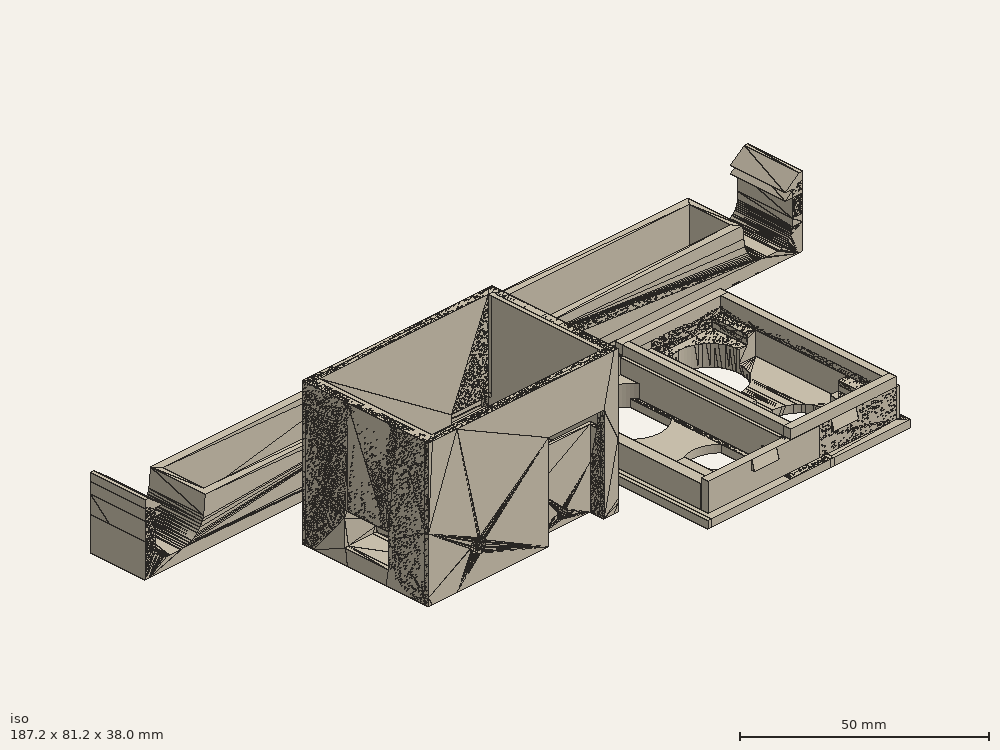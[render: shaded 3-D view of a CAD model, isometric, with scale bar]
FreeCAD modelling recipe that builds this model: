
FCSTD DOCUMENT  (FreeCAD 0.18.4R)
Label: station.sensor
License: All rights reserved
LicenseURL: http://en.wikipedia.org/wiki/All_rights_reserved
objects: Part::Extrusion×50, Part::Feature×48, Part::MultiFuse×25, Part::Cut×23, Part::Part2DObjectPython×19, Part::FeaturePython×15, App::DocumentObjectGroup×5
note: 180 computed .brp shape members not serialized (recipe doc carries the construction recipe); baked Part::Feature solids carry a one-line shape summary decoded from their .brp

FEATURE [Part::Feature] Cut004008021006004001003001  label="Cut004008021006004001004"
  shape: bbox 187.2 x 15.6 x 18.67 mm, 52 faces, 2 solids (baked)
FEATURE [Part::Feature] Fusion005002002014004003003002009002010004002003006003008008004007002004008002005003003004013003004015001  label="Fusion005002002014004003003002009002010004002003006003008008004007002004008002005003003004013003004019"
  shape: bbox 54 x 34.03 x 38 mm, 82 faces (baked)
FEATURE [Part::Feature] Cut004008021006004001001  label="Cut004008021006006"
  shape: bbox 34.03 x 54 x 8 mm, 44 faces (baked)
FEATURE [Part::Part2DObjectPython] Wire  # Draft 2D object (typed FeaturePython)
  ChamferSize = 0
  Closed = true
  End = (195.757,-75.1327,-187.001)
  FilletRadius = 0
  Length = 25.2
  MakeFace = true
  Placement = pos=(193.657,-71.4954,-187.001) rot=(0,0,1;0rad)
  Points = (6) [(0,0,0),(2.1,3.63731,0),(6.3,3.63731,0),(8.4,0,0),(6.3,-3.63731,0),(2.1,-3.63731,2.84217e-14)]
  Start = (193.657,-71.4954,-187.001)
  Subdivisions = 0
FEATURE [Part::Feature] Face
  shape: bbox 10 x 11.6 x 0.0004728 mm, 1 faces, 0 solids (baked)
FEATURE [Part::Extrusion] Extrusion
  Base = -> Face
  Dir = (3e-15,1.7e-14,1)
  DirMode = 0
  FaceMakerClass = Part::FaceMakerBullseye
  LengthFwd = 0
  LengthRev = 0
  Solid = true
  Symmetric = false
FEATURE [Part::Cut] Cut
  Base = -> Cut004008021006004001003001
  Tool = -> Extrusion
FEATURE [Part::Feature] Face001
  Placement = pos=(3e-15,1.7e-14,1) rot=(0,0,1;0rad)
  shape: bbox 10 x 11.6 x 0.0004728 mm, 1 faces, 0 solids (baked)
FEATURE [Part::Extrusion] Extrusion001
  Base = -> Face001
  Dir = (-1.05e-14,-5.95e-14,-3.5)
  DirMode = 0
  FaceMakerClass = Part::FaceMakerBullseye
  LengthFwd = 0
  LengthRev = 0
  Solid = true
  Symmetric = false
FEATURE [Part::Extrusion] Extrusion002
  Base = -> Wire
  Dir = (3.9e-15,8.4e-15,3.5)
  DirMode = 0
  FaceMakerClass = Part::FaceMakerBullseye
  LengthFwd = 0
  LengthRev = 0
  Solid = true
  Symmetric = false
FEATURE [Part::Cut] Cut004008021006004001003002
  Base = -> Extrusion001
  Tool = -> Extrusion002
FEATURE [Part::MultiFuse] Fusion
  Shapes = -> [Cut004008021006004001003002,Cut]
FEATURE [Part::Part2DObjectPython] Rectangle  # Draft 2D object (typed FeaturePython)
  ChamferSize = 0
  Columns = 1
  FilletRadius = 0
  Height = 2.16
  Length = 2.16
  MakeFace = true
  Placement = pos=(202.857,-77.2954,-189.161) rot=(0.57735,0.57735,0.57735;2.0944rad)
  Rows = 1
  Support = -> [Fusion]
FEATURE [Part::Extrusion] Extrusion003
  Base = -> Rectangle
  Dir = (-10,0,0)
  DirMode = 0
  FaceMakerClass = Part::FaceMakerBullseye
  LengthFwd = 0
  LengthRev = 0
  Placement = pos=(0,9.44,-1.99e-13) rot=(0,0,1;0rad)
  Solid = true
  Symmetric = false
FEATURE [Part::Extrusion] Extrusion004
  Base = -> Rectangle
  Dir = (-10,0,0)
  DirMode = 0
  FaceMakerClass = Part::FaceMakerBullseye
  LengthFwd = 0
  LengthRev = 0
  Solid = true
  Symmetric = false
FEATURE [Part::Part2DObjectPython] Circle  # Draft 2D object (typed FeaturePython)
  FirstAngle = 0
  LastAngle = 0
  MakeFace = true
  Placement = pos=(202.857,-67.8554,-189.161) rot=(0.57735,0.57735,0.57735;2.0944rad)
  Radius = 2.16
  Support = -> [Extrusion003]
FEATURE [Part::Extrusion] Extrusion005
  Base = -> Circle
  Dir = (-10,0,0)
  DirMode = 0
  FaceMakerClass = Part::FaceMakerBullseye
  LengthFwd = 0
  LengthRev = 0
  Solid = true
  Symmetric = false
FEATURE [Part::Extrusion] Extrusion006
  Base = -> Circle
  Dir = (-10,0,0)
  DirMode = 0
  FaceMakerClass = Part::FaceMakerBullseye
  LengthFwd = 0
  LengthRev = 0
  Placement = pos=(0,-7.28,1.99e-13) rot=(0,0,1;0rad)
  Solid = true
  Symmetric = false
FEATURE [Part::Cut] Cut004008021006004001003003
  Base = -> Extrusion003
  Tool = -> Extrusion005
FEATURE [Part::Cut] Cut004008021006004001003004
  Base = -> Extrusion004
  Tool = -> Extrusion006
FEATURE [Part::MultiFuse] Fusion005002002014004003003002009002010004002003006003008008004007002004008002005003003004013003004015002
  Placement = pos=(-5.94964,-41.2662,-1.6816e-09) rot=(0,0,1;0rad)
  Shapes = -> [Cut004008021006004001003003,Cut004008021006004001003004,Fusion]
FEATURE [Part::Part2DObjectPython] Rectangle001  # Draft 2D object (typed FeaturePython)
  ChamferSize = 0
  Columns = 1
  FilletRadius = 0
  Height = 2
  Length = 21
  MakeFace = true
  Placement = pos=(223.104,-136.121,-186.001) rot=(0,0,1;0rad)
  Rows = 1
FEATURE [Part::Extrusion] Extrusion007
  Base = -> Rectangle001
  Dir = (3e-16,0,-3.5)
  DirMode = 0
  FaceMakerClass = Part::FaceMakerBullseye
  LengthFwd = 0
  LengthRev = 0
  Solid = true
  Symmetric = false
FEATURE [Part::Feature] Face002
  Placement = pos=(223.104,-136.121,-186.001) rot=(0,0,1;0rad)
  shape: bbox 21 x 2 x 2e-07 mm, 1 faces, 0 solids (baked)
FEATURE [Part::Extrusion] Extrusion008
  Base = -> Face002
  Dir = (-2e-16,0,2.5)
  DirMode = 0
  FaceMakerClass = Part::FaceMakerBullseye
  LengthFwd = 0
  LengthRev = 0
  Solid = true
  Symmetric = false
FEATURE [Part::MultiFuse] Fusion005002002014004003003002009002010004002003006003008008004007002004008002005003003004013003004015003
  Shapes = -> [Extrusion008,Extrusion007]
FEATURE [Part::Feature] Fusion005002002014004003003002009002010004002003006003008008004007002004008002005003003004013003004015003001  label="Fusion005002002014004003003002009002010004002003006003008008004007002004008002005003003004013003004015004"
  shape: bbox 21 x 2 x 6 mm, 6 faces (baked)
FEATURE [Part::Feature] Face003
  shape: bbox 2e-07 x 2 x 6 mm, 1 faces, 0 solids (baked)
FEATURE [Part::Extrusion] Extrusion009
  Base = -> Face003
  Dir = (4.51897,0,0)
  DirMode = 0
  FaceMakerClass = Part::FaceMakerBullseye
  LengthFwd = 0
  LengthRev = 0
  Solid = true
  Symmetric = false
FEATURE [Part::Feature] Face004
  shape: bbox 2e-07 x 2 x 6 mm, 1 faces, 0 solids (baked)
FEATURE [Part::Extrusion] Extrusion010
  Base = -> Face004
  Dir = (-4.50603,0,0)
  DirMode = 0
  FaceMakerClass = Part::FaceMakerBullseye
  LengthFwd = 0
  LengthRev = 0
  Solid = true
  Symmetric = false
FEATURE [Part::MultiFuse] Fusion005002002014004003003002009002010004002003006003008008004007002004008002005003003004013003004015003002
  Shapes = -> [Fusion005002002014004003003002009002010004002003006003008008004007002004008002005003003004013003004015003001,Extrusion010,Extrusion009]
FEATURE [Part::Feature] Fusion005002002014004003003002009002010004002003006003008008004007002004008002005003003004013003004015003002001  label="Fusion005002002014004003003002009002010004002003006003008008004007002004008002005003003004013003004015003003"
  Placement = pos=(0,-48,0) rot=(0,0,1;0rad)
  shape: bbox 30.03 x 2 x 6 mm, 6 faces (baked)
FEATURE [Part::Feature] Fusion005002002014004003003002009002010004002003006003008008004007002004008002005003003004013003004015003002002  label="Fusion005002002014004003003002009002010004002003006003008008004007002004008002005003003004013003004015003004"
  shape: bbox 30.03 x 2 x 6 mm, 6 faces (baked)
FEATURE [Part::Feature] Face005
  Placement = pos=(0,-48,0) rot=(0,0,1;0rad)
  shape: bbox 30.03 x 2 x 2e-07 mm, 1 faces, 0 solids (baked)
FEATURE [Part::Extrusion] Extrusion011
  Base = -> Face005
  Dir = (0,0,4)
  DirMode = 0
  FaceMakerClass = Part::FaceMakerBullseye
  LengthFwd = 0
  LengthRev = 0
  Solid = true
  Symmetric = false
FEATURE [Part::Feature] Face006
  shape: bbox 30.03 x 2 x 2e-07 mm, 1 faces, 0 solids (baked)
FEATURE [Part::Extrusion] Extrusion012
  Base = -> Face006
  Dir = (0,0,4)
  DirMode = 0
  FaceMakerClass = Part::FaceMakerBullseye
  LengthFwd = 0
  LengthRev = 0
  Solid = true
  Symmetric = false
FEATURE [Part::MultiFuse] Fusion005002002014004003003002009002010004002003006003008008004007002004008002005003003004013003004015003002003
  Shapes = -> [Fusion005002002014004003003002009002010004002003006003008008004007002004008002005003003004013003004015003002002,Extrusion012]
FEATURE [Part::MultiFuse] Fusion005002002014004003003002009002010004002003006003008008004007002004008002005003003004013003004015003002004
  Shapes = -> [Fusion005002002014004003003002009002010004002003006003008008004007002004008002005003003004013003004015003002001,Extrusion011]
FEATURE [Part::Part2DObjectPython] Rectangle002  # Draft 2D object (typed FeaturePython)
  ChamferSize = 0
  Columns = 1
  FilletRadius = 0
  Height = 2
  Length = 46
  MakeFace = true
  Placement = pos=(220.598,-182.121,-183.501) rot=(0,0,1;1.5708rad)
  Rows = 1
FEATURE [Part::Extrusion] Extrusion013
  Base = -> Rectangle002
  Dir = (1.04e-14,1.04e-14,4)
  DirMode = 0
  FaceMakerClass = Part::FaceMakerBullseye
  LengthFwd = 0
  LengthRev = 0
  Solid = true
  Symmetric = false
FEATURE [Part::Feature] Face007
  Placement = pos=(220.598,-182.121,-183.501) rot=(0,0,1;1.5708rad)
  shape: bbox 2 x 46 x 1.04e-05 mm, 1 faces, 0 solids (baked)
FEATURE [Part::Extrusion] Extrusion014
  Base = -> Face007
  Dir = (-1.57e-14,-1.57e-14,-6)
  DirMode = 0
  FaceMakerClass = Part::FaceMakerBullseye
  LengthFwd = 0
  LengthRev = 0
  Solid = true
  Symmetric = false
FEATURE [Part::MultiFuse] Fusion005002002014004003003002009002010004002003006003008008004007002004008002005003003004013003004015003002005
  Placement = pos=(28.025,0,1.421e-13) rot=(0,0,1;0rad)
  Shapes = -> [Extrusion014,Extrusion013]
FEATURE [Part::MultiFuse] Fusion005002002014004003003002009002010004002003006003008008004007002004008002005003003004013003004015003002006
  Shapes = -> [Extrusion014,Extrusion013]
FEATURE [Part::MultiFuse] Fusion005002002014004003003002009002010004002003006003008008004007002004008002005003003004013003004015003002007
  Shapes = -> [Cut004008021006004001001,Fusion005002002014004003003002009002010004002003006003008008004007002004008002005003003004013003004015003002005,Fusion005002002014004003003002009002010004002003006003008008004007002004008002005003003004013003004015003002006]
FEATURE [Part::MultiFuse] Fusion005002002014004003003002009002010004002003006003008008004007002004008002005003003004013003004015003002008
  Shapes = -> [Fusion005002002014004003003002009002010004002003006003008008004007002004008002005003003004013003004015003002003,Fusion005002002014004003003002009002010004002003006003008008004007002004008002005003003004013003004015003002004,Fusion005002002014004003003002009002010004002003006003008008004007002004008002005003003004013003004015003002007]
FEATURE [Part::Feature] Fusion005002002014004003003002009002010004002003006003008008004007002004008002005003003004013003004015003002008001  label="Fusion005002002014004003003002009002010004002003006003008008004007002004008002005003003004013003004015003002009"
  shape: bbox 34.03 x 54 x 12 mm, 48 faces (baked)
FEATURE [Part::Feature] Face008
  shape: bbox 54 x 0.0001893 x 38 mm, 1 faces, 0 solids (baked)
FEATURE [Part::Extrusion] Extrusion015
  Base = -> Face008
  Dir = (2.72249e-11,-1,-4.64269e-10)
  DirMode = 0
  FaceMakerClass = Part::FaceMakerBullseye
  LengthFwd = 0
  LengthRev = 0
  Solid = true
  Symmetric = false
FEATURE [Part::Part2DObjectPython] Rectangle003  # Draft 2D object (typed FeaturePython)
  ChamferSize = 0
  Columns = 1
  FilletRadius = 0
  Height = 1
  Length = 48
  MakeFace = true
  Placement = pos=(133.985,-166.503,-153.501) rot=(0,0,1;0rad)
  Rows = 1
FEATURE [Part::Extrusion] Extrusion016
  Base = -> Rectangle003
  Dir = (3.41957e-08,1.53606e-08,-17.6)
  DirMode = 0
  FaceMakerClass = Part::FaceMakerBullseye
  LengthFwd = 0
  LengthRev = 0
  Solid = true
  Symmetric = false
FEATURE [Part::Cut] Cut004008021006004001003005
  Base = -> Fusion005002002014004003003002009002010004002003006003008008004007002004008002005003003004013003004015001
  Tool = -> Extrusion016
FEATURE [Part::Feature] Face009
  shape: bbox 30.3 x 0.00019 x 8.9 mm, 1 faces, 0 solids (baked)
FEATURE [Part::Extrusion] Extrusion017
  Base = -> Face009
  Dir = (9.5e-15,-1,1.93e-14)
  DirMode = 0
  FaceMakerClass = Part::FaceMakerBullseye
  LengthFwd = 0
  LengthRev = 0
  Solid = true
  Symmetric = false
FEATURE [Part::Cut] Cut004008021006004001003006
  Base = -> Cut004008021006004001003005
  Tool = -> Extrusion017
FEATURE [Part::MultiFuse] Fusion005002002014004003003002009002010004002003006003008008004007002004008002005003003004013003004015003002008002
  Shapes = -> [Extrusion015,Cut004008021006004001003006]
FEATURE [Part::Feature] Face010
  Placement = pos=(-3.901e-12,0.075,3.0967e-11) rot=(0,0,1;0rad)
  shape: bbox 54 x 0.0001896 x 38 mm, 1 faces, 0 solids (baked)
FEATURE [Part::Extrusion] Extrusion018
  Base = -> Face010
  Dir = (-4.81063e-11,0.925,3.81925e-10)
  DirMode = 0
  FaceMakerClass = Part::FaceMakerBullseye
  LengthFwd = 0
  LengthRev = 0
  Solid = true
  Symmetric = false
FEATURE [Part::MultiFuse] Fusion005002002014004003003002009002010004002003006003008008004007002004008002005003003004013003004015003002008003
  Shapes = -> [Fusion005002002014004003003002009002010004002003006003008008004007002004008002005003003004013003004015003002008002,Extrusion018]
FEATURE [Part::Feature] Face011
  shape: bbox 10.5 x 0.0001898 x 10.5 mm, 1 faces, 0 solids (baked)
FEATURE [Part::Extrusion] Extrusion019
  Base = -> Face011
  Dir = (-5.39565e-11,1.0375,4.28378e-10)
  DirMode = 0
  FaceMakerClass = Part::FaceMakerBullseye
  LengthFwd = 0
  LengthRev = 0
  Solid = true
  Symmetric = false
FEATURE [Part::Feature] Face012
  shape: bbox 48 x 0.0001898 x 26.5 mm, 1 faces, 0 solids (baked)
FEATURE [Part::Extrusion] Extrusion020
  Base = -> Face012
  Dir = (-1.32012e-11,0.925,1.56655e-11)
  DirMode = 0
  FaceMakerClass = Part::FaceMakerBullseye
  LengthFwd = 0
  LengthRev = 0
  Solid = true
  Symmetric = false
FEATURE [Part::Cut] Cut004008021006004001003007
  Base = -> Fusion005002002014004003003002009002010004002003006003008008004007002004008002005003003004013003004015003002008003
  Tool = -> Extrusion020
FEATURE [Part::Feature] Cut004008021006004001003007001  label="Cut004008021006004001003008"
  shape: bbox 54 x 35.95 x 38 mm, 83 faces (baked)
FEATURE [Part::Part2DObjectPython] Rectangle004  # Draft 2D object (typed FeaturePython)
  ChamferSize = 0
  Columns = 1
  FilletRadius = 0
  Height = 2.6
  Length = 7.5
  MakeFace = true
  Placement = pos=(133.985,-146.703,-160.901) rot=(0.57735,-0.57735,-0.57735;2.0944rad)
  Rows = 1
FEATURE [Part::Part2DObjectPython] Rectangle005  # Draft 2D object (typed FeaturePython)
  ChamferSize = 0
  Columns = 1
  FilletRadius = 0
  Height = 2.6
  Length = 7.5
  MakeFace = true
  Placement = pos=(181.985,-146.703,-160.901) rot=(0.57735,-0.57735,-0.57735;2.0944rad)
  Rows = 1
FEATURE [Part::Extrusion] Extrusion021
  Base = -> Rectangle005
  Dir = (1,0,0)
  DirMode = 0
  FaceMakerClass = Part::FaceMakerBullseye
  LengthFwd = 0
  LengthRev = 0
  Solid = true
  Symmetric = false
FEATURE [Part::Cut] Cut004008021006004001003007002
  Base = -> Cut004008021006004001003007001
  Tool = -> Extrusion021
FEATURE [Part::Extrusion] Extrusion022
  Base = -> Rectangle004
  Dir = (-1,0,0)
  DirMode = 0
  FaceMakerClass = Part::FaceMakerBullseye
  LengthFwd = 0
  LengthRev = 0
  Solid = true
  Symmetric = false
FEATURE [Part::Cut] Cut004008021006004001003007003
  Base = -> Cut004008021006004001003007002
  Tool = -> Extrusion022
FEATURE [Part::FeaturePython] Slice001_child0  label="Slice001.0"  # WARN: FeaturePython — macro-defined, semantics opaque (R4)
  FilterType = 1
  Invert = false
  OverrideMaxVal = 0
  Placement = pos=(518.285,135.789,-184.867) rot=(0,0,1;1.5708rad)
  WindowFrom = 80
  WindowTo = 100
  items = 0
FEATURE [Part::FeaturePython] Slice_child2  label="Slice.2"  # WARN: FeaturePython — macro-defined, semantics opaque (R4)
  FilterType = 1
  Invert = false
  OverrideMaxVal = 0
  Placement = pos=(518.285,128.495,-184.867) rot=(0,0,1;1.5708rad)
  WindowFrom = 80
  WindowTo = 100
  items = 2
FEATURE [Part::Feature] Face013
  shape: bbox 30.03 x 50 x 1.04e-05 mm, 1 faces, 0 solids (baked)
FEATURE [Part::Extrusion] Extrusion023
  Base = -> Face013
  Dir = (7.5e-15,-3.1e-15,-2.5)
  DirMode = 0
  FaceMakerClass = Part::FaceMakerBullseye
  LengthFwd = 0
  LengthRev = 0
  Solid = true
  Symmetric = false
FEATURE [Part::Cut] Cut004008021006004001003007004
  Base = -> Fusion005002002014004003003002009002010004002003006003008008004007002004008002005003003004013003004015003002008001
  Tool = -> Extrusion023
FEATURE [Part::MultiFuse] Fusion005002002014004003003002009002010004002003006003008008004007002004008002005003003004013003004015003002008004
  Shapes = -> [Slice001_child0,Cut004008021006004001003007004]
FEATURE [Part::MultiFuse] Fusion005002002014004003003002009002010004002003006003008008004007002004008002005003003004013003004015003002008005
  Shapes = -> [Fusion005002002014004003003002009002010004002003006003008008004007002004008002005003003004013003004015003002008004,Slice_child2]
FEATURE [Part::Part2DObjectPython] Rectangle006  # Draft 2D object (typed FeaturePython)
  ChamferSize = 0
  Columns = 1
  FilletRadius = 0
  Height = 0.3
  Length = 30.025
  MakeFace = true
  Placement = pos=(218.598,-136.421,-182.001) rot=(0,0,1;0rad)
  Rows = 1
FEATURE [Part::Extrusion] Extrusion024
  Base = -> Rectangle006
  Dir = (2.24e-14,-9.2e-15,-7.5)
  DirMode = 0
  FaceMakerClass = Part::FaceMakerBullseye
  LengthFwd = 0
  LengthRev = 0
  Solid = true
  Symmetric = false
FEATURE [Part::Cut] Cut004008021006004001003007005
  Base = -> Fusion005002002014004003003002009002010004002003006003008008004007002004008002005003003004013003004015003002008005
  Tool = -> Extrusion024
FEATURE [Part::Part2DObjectPython] Rectangle007  # Draft 2D object (typed FeaturePython)
  ChamferSize = 0
  Columns = 1
  FilletRadius = 0
  Height = 0.3
  Length = 30.025
  MakeFace = true
  Placement = pos=(218.598,-182.121,-182.001) rot=(0,0,1;0rad)
  Rows = 1
FEATURE [Part::Extrusion] Extrusion025
  Base = -> Rectangle007
  Dir = (2.24e-14,-9.2e-15,-7.5)
  DirMode = 0
  FaceMakerClass = Part::FaceMakerBullseye
  LengthFwd = 0
  LengthRev = 0
  Solid = true
  Symmetric = false
FEATURE [Part::Cut] Cut004008021006004001003007006
  Base = -> Cut004008021006004001003007005
  Tool = -> Extrusion025
FEATURE [Part::Feature] Face014
  shape: bbox 1.036e-05 x 2 x 7.5 mm, 1 faces, 0 solids (baked)
FEATURE [Part::Extrusion] Extrusion026
  Base = -> Face014
  Dir = (0.8375,1.8e-15,-4.1e-15)
  DirMode = 0
  FaceMakerClass = Part::FaceMakerBullseye
  LengthFwd = 0
  LengthRev = 0
  Solid = true
  Symmetric = false
FEATURE [Part::Feature] Face015
  shape: bbox 1.036e-05 x 2 x 7.5 mm, 1 faces, 0 solids (baked)
FEATURE [Part::Extrusion] Extrusion027
  Base = -> Face015
  Dir = (-0.8375,-2e-15,1.41e-14)
  DirMode = 0
  FaceMakerClass = Part::FaceMakerBullseye
  LengthFwd = 0
  LengthRev = 0
  Solid = true
  Symmetric = false
FEATURE [Part::MultiFuse] Fusion005002002014004003003002009002010004002003006003008008004007002004008002005003003004013003004015003002008006
  Shapes = -> [Cut004008021006004001003007006,Extrusion026,Extrusion027]
FEATURE [Part::Feature] Face016
  shape: bbox 1.036e-05 x 2 x 7.5 mm, 1 faces, 0 solids (baked)
FEATURE [Part::Extrusion] Extrusion028
  Base = -> Face016
  Dir = (0.8375,1.8e-15,-4.1e-15)
  DirMode = 0
  FaceMakerClass = Part::FaceMakerBullseye
  LengthFwd = 0
  LengthRev = 0
  Solid = true
  Symmetric = false
FEATURE [Part::Feature] Face017
  shape: bbox 1.036e-05 x 2 x 7.5 mm, 1 faces, 0 solids (baked)
FEATURE [Part::Extrusion] Extrusion029
  Base = -> Face017
  Dir = (-0.8375,-2e-15,1.41e-14)
  DirMode = 0
  FaceMakerClass = Part::FaceMakerBullseye
  LengthFwd = 0
  LengthRev = 0
  Solid = true
  Symmetric = false
FEATURE [Part::MultiFuse] Fusion005002002014004003003002009002010004002003006003008008004007002004008002005003003004013003004015003002008007
  Shapes = -> [Fusion005002002014004003003002009002010004002003006003008008004007002004008002005003003004013003004015003002008006,Extrusion029,Extrusion028]
FEATURE [Part::Feature] Face018
  shape: bbox 1.036e-05 x 45.4 x 7.5 mm, 1 faces, 0 solids (baked)
FEATURE [Part::Extrusion] Extrusion030
  Base = -> Face018
  Dir = (0.8375,1.8e-15,-4.1e-15)
  DirMode = 0
  FaceMakerClass = Part::FaceMakerBullseye
  LengthFwd = 0
  LengthRev = 0
  Solid = true
  Symmetric = false
FEATURE [Part::MultiFuse] Fusion005002002014004003003002009002010004002003006003008008004007002004008002005003003004013003004015003002008008
  Shapes = -> [Fusion005002002014004003003002009002010004002003006003008008004007002004008002005003003004013003004015003002008007,Extrusion030]
FEATURE [Part::Feature] Face019
  shape: bbox 1.036e-05 x 45.4 x 7.5 mm, 1 faces, 0 solids (baked)
FEATURE [Part::Extrusion] Extrusion031
  Base = -> Face019
  Dir = (-0.8375,-2e-15,1.41e-14)
  DirMode = 0
  FaceMakerClass = Part::FaceMakerBullseye
  LengthFwd = 0
  LengthRev = 0
  Solid = true
  Symmetric = false
FEATURE [Part::MultiFuse] Fusion005002002014004003003002009002010004002003006003008008004007002004008002005003003004013003004015003002008009
  Shapes = -> [Fusion005002002014004003003002009002010004002003006003008008004007002004008002005003003004013003004015003002008008,Extrusion031]
FEATURE [Part::Feature] Fusion005002002014004003003002009002010004002003006003008008004007002004008002005003003004013003004015003002008009001  label="Fusion005002002014004003003002009002010004002003006003008008004007002004008002005003003004013003004015003002008010"
  shape: bbox 34.03 x 54 x 9.5 mm, 65 faces (baked)
FEATURE [Part::Part2DObjectPython] Rectangle008  # Draft 2D object (typed FeaturePython)
  ChamferSize = 0
  Columns = 1
  FilletRadius = 0
  Height = 2.8375
  Length = 15.7
  MakeFace = true
  Placement = pos=(249.46,-181.821,-182.001) rot=(0,0,1;1.5708rad)
  Rows = 1
FEATURE [Part::Extrusion] Extrusion032
  Base = -> Rectangle008
  Dir = (-2.96e-14,-3.82e-14,-7.5)
  DirMode = 0
  FaceMakerClass = Part::FaceMakerBullseye
  LengthFwd = 0
  LengthRev = 0
  Solid = true
  Symmetric = false
FEATURE [Part::Cut] Cut004008021006004001003007007
  Base = -> Fusion005002002014004003003002009002010004002003006003008008004007002004008002005003003004013003004015003002008009001
  Tool = -> Extrusion032
FEATURE [Part::Feature] Face022
  shape: bbox 2.838 x 29.7 x 1.05e-05 mm, 1 faces, 0 solids (baked)
FEATURE [Part::Extrusion] Extrusion033
  Base = -> Face022
  Dir = (-1.45e-14,-1.7e-15,-1.5)
  DirMode = 0
  FaceMakerClass = Part::FaceMakerBullseye
  LengthFwd = 0
  LengthRev = 0
  Solid = true
  Symmetric = false
FEATURE [Part::Cut] Cut004008021006004001003007008
  Base = -> Cut004008021006004001003007007
  Tool = -> Extrusion033
FEATURE [Part::Feature] Face023
  shape: bbox 2.838 x 45.4 x 1.05e-05 mm, 1 faces, 0 solids (baked)
FEATURE [Part::Extrusion] Extrusion034
  Base = -> Face023
  Dir = (-5.07e-14,-2.2e-15,-1.5)
  DirMode = 0
  FaceMakerClass = Part::FaceMakerBullseye
  LengthFwd = 0
  LengthRev = 0
  Solid = true
  Symmetric = false
FEATURE [Part::Cut] Cut004008021006004001003007009
  Base = -> Cut004008021006004001003007008
  Placement = pos=(-22.7066,-0.0612293,5.22621e-08) rot=(0,0,1;0rad)
  Tool = -> Extrusion034
FEATURE [Part::Feature] Face029
  shape: bbox 0.0001899 x 33.95 x 37 mm, 1 faces, 0 solids (baked)
FEATURE [Part::Extrusion] Extrusion035
  Base = -> Face029
  Dir = (1.1,6.46386e-10,8.56453e-10)
  DirMode = 0
  FaceMakerClass = Part::FaceMakerBullseye
  LengthFwd = 0
  LengthRev = 0
  Solid = true
  Symmetric = false
FEATURE [Part::Feature] Face030
  shape: bbox 0.0001899 x 31.95 x 24.13 mm, 1 faces, 0 solids (baked)
FEATURE [Part::Extrusion] Extrusion036
  Base = -> Face030
  Dir = (-1.1,-2.23033e-10,-1.23176e-09)
  DirMode = 0
  FaceMakerClass = Part::FaceMakerBullseye
  LengthFwd = 0
  LengthRev = 0
  Solid = true
  Symmetric = false
FEATURE [Part::Cut] Cut004008021006004001003007010
  Base = -> Cut004008021006004001003007003
  Tool = -> Extrusion035
FEATURE [Part::Cut] Cut004008021006004001003007011
  Base = -> Cut004008021006004001003007010
  Tool = -> Extrusion036
FEATURE [Part::Feature] Face031
  shape: bbox 1.1 x 1.963 x 0.0001898 mm, 1 faces, 0 solids (baked)
FEATURE [Part::Extrusion] Extrusion037
  Base = -> Face031
  Dir = (-1.03553e-08,-5.49146e-09,13.3)
  DirMode = 0
  FaceMakerClass = Part::FaceMakerBullseye
  LengthFwd = 0
  LengthRev = 0
  Solid = true
  Symmetric = false
FEATURE [Part::MultiFuse] Fusion005002002014004003003002009002010004002003006003008008004007002004008002005003003004013003004015003002008009002
  Shapes = -> [Extrusion037,Cut004008021006004001003007011]
FEATURE [Part::Feature] Fusion005002002014004003003002009002010004002003006003008008004007002004008002005003003004013003004015003002008009002001  label="Fusion005002002014004003003002009002010004002003006003008008004007002004008002005003003004013003004015003002008009003"
  shape: bbox 54 x 35.95 x 38 mm, 95 faces (baked)
FEATURE [Part::Feature] Face032
  Placement = pos=(132.985,-146.703,-160.901) rot=(0.57735,-0.57735,-0.57735;2.0944rad)
  shape: bbox 0.0001898 x 7.5 x 2.6 mm, 1 faces, 0 solids (baked)
FEATURE [Part::Extrusion] Extrusion038
  Base = -> Face032
  Dir = (-1.1,0,0)
  DirMode = 0
  FaceMakerClass = Part::FaceMakerBullseye
  LengthFwd = 0
  LengthRev = 0
  Solid = true
  Symmetric = false
FEATURE [Part::Feature] Face033
  Placement = pos=(182.985,-146.703,-160.901) rot=(0.57735,-0.57735,-0.57735;2.0944rad)
  shape: bbox 0.0001898 x 7.5 x 2.6 mm, 1 faces, 0 solids (baked)
FEATURE [Part::Extrusion] Extrusion039
  Base = -> Face033
  Dir = (1.1,0,0)
  DirMode = 0
  FaceMakerClass = Part::FaceMakerBullseye
  LengthFwd = 0
  LengthRev = 0
  Solid = true
  Symmetric = false
FEATURE [Part::Cut] Cut004008021006004001003007012
  Base = -> Fusion005002002014004003003002009002010004002003006003008008004007002004008002005003003004013003004015003002008009002001
  Tool = -> Extrusion039
FEATURE [Part::Cut] Cut004008021006004001003007013
  Base = -> Cut004008021006004001003007012
  Tool = -> Extrusion038
FEATURE [Part::Feature] Face038
  Placement = pos=(-5.94964,-41.2662,-1.6816e-09) rot=(0,0,1;0rad)
  shape: bbox 0.0004728 x 2 x 2 mm, 1 faces, 0 solids (baked)
FEATURE [Part::Extrusion] Extrusion040
  Base = -> Face038
  Dir = (-1.1,0,3.1e-15)
  DirMode = 0
  FaceMakerClass = Part::FaceMakerBullseye
  LengthFwd = 0
  LengthRev = 0
  Solid = true
  Symmetric = false
FEATURE [Part::Feature] Face039
  Placement = pos=(-5.94964,-41.2662,-1.6816e-09) rot=(0,0,1;0rad)
  shape: bbox 0.0004728 x 2 x 2 mm, 1 faces, 0 solids (baked)
FEATURE [Part::Extrusion] Extrusion041
  Base = -> Face039
  Dir = (-1.1,0,3.1e-15)
  DirMode = 0
  FaceMakerClass = Part::FaceMakerBullseye
  LengthFwd = 0
  LengthRev = 0
  Solid = true
  Symmetric = false
FEATURE [Part::Feature] Face040
  Placement = pos=(-5.94964,-41.2662,-1.6816e-09) rot=(0,0,1;0rad)
  shape: bbox 0.0004728 x 2 x 2 mm, 1 faces, 0 solids (baked)
FEATURE [Part::Extrusion] Extrusion042
  Base = -> Face040
  Dir = (1.1,0,-3.1e-15)
  DirMode = 0
  FaceMakerClass = Part::FaceMakerBullseye
  LengthFwd = 0
  LengthRev = 0
  Solid = true
  Symmetric = false
FEATURE [Part::Feature] Face041
  Placement = pos=(-5.94964,-41.2662,-1.6816e-09) rot=(0,0,1;0rad)
  shape: bbox 0.0004728 x 2 x 2 mm, 1 faces, 0 solids (baked)
FEATURE [Part::Extrusion] Extrusion043
  Base = -> Face041
  Dir = (1.1,0,-3.1e-15)
  DirMode = 0
  FaceMakerClass = Part::FaceMakerBullseye
  LengthFwd = 0
  LengthRev = 0
  Solid = true
  Symmetric = false
FEATURE [Part::MultiFuse] Fusion005002002014004003003002009002010004002003006003008008004007002004008002005003003004013003004015003002008009002002
  Shapes = -> [Extrusion040,Extrusion041,Extrusion042,Extrusion043]
FEATURE [Part::Cut] Cut004008021006004001003007014
  Base = -> Fusion005002002014004003003002009002010004002003006003008008004007002004008002005003003004013003004015002
  Tool = -> Fusion005002002014004003003002009002010004002003006003008008004007002004008002005003003004013003004015003002008009002002
FEATURE [Part::Feature] Cut004008021006004001003007014001  label="Cut004008021006004001003007015"
  shape: bbox 187.2 x 15.6 x 18.67 mm, 61 faces, 2 solids (baked)
FEATURE [Part::Part2DObjectPython] Rectangle009  # Draft 2D object (typed FeaturePython)
  ChamferSize = 0
  Columns = 1
  FilletRadius = 0
  Height = 1
  Length = 5
  MakeFace = true
  Placement = pos=(130.985,-148.403,-154.501) rot=(0.57735,-0.57735,-0.57735;2.0944rad)
  Rows = 1
FEATURE [Part::Extrusion] Extrusion044
  Base = -> Rectangle009
  Dir = (67.7585,0,0)
  DirMode = 0
  FaceMakerClass = Part::FaceMakerBullseye
  LengthFwd = 0
  LengthRev = 0
  Solid = true
  Symmetric = false
FEATURE [Part::Cut] Cut004008021006004001003007014002
  Base = -> Cut004008021006004001003007013
  Tool = -> Extrusion044
FEATURE [Part::Part2DObjectPython] Circle001  # Draft 2D object (typed FeaturePython)
  FirstAngle = 0
  LastAngle = 0
  MakeFace = true
  Placement = pos=(168.62,-144.553,-189.501) rot=(0,0,1;0rad)
  Radius = 1.5001
  Support = -> [Cut004008021006004001003007014002]
FEATURE [Part::Part2DObjectPython] Circle002  # Draft 2D object (typed FeaturePython)
  FirstAngle = 0
  LastAngle = 0
  MakeFace = true
  Placement = pos=(168.62,-144.553,-189.501) rot=(0,0,1;0rad)
  Radius = 2
  Support = -> [Circle001]
FEATURE [Part::Extrusion] Extrusion045
  Base = -> Circle001
  Dir = (5.09097e-10,9.78257e-11,2.33988)
  DirMode = 0
  FaceMakerClass = Part::FaceMakerBullseye
  LengthFwd = 0
  LengthRev = 0
  Solid = true
  Symmetric = false
FEATURE [Part::Extrusion] Extrusion046
  Base = -> Circle002
  Dir = (5.09097e-10,9.78257e-11,2.33988)
  DirMode = 0
  FaceMakerClass = Part::FaceMakerBullseye
  LengthFwd = 0
  LengthRev = 0
  Solid = true
  Symmetric = false
FEATURE [Part::Cut] Cut004008021006004001003007014003
  Base = -> Extrusion046
  Tool = -> Extrusion045
FEATURE [Part::Feature] Face042
  shape: bbox 4 x 4 x 2.009e-07 mm, 1 faces, 0 solids (baked)
FEATURE [Part::Extrusion] Extrusion047
  Base = -> Face042
  Dir = (-2.17574e-10,-4.1808e-11,-1)
  DirMode = 0
  FaceMakerClass = Part::FaceMakerBullseye
  LengthFwd = 0
  LengthRev = 0
  Solid = true
  Symmetric = false
FEATURE [Part::Cut] Cut004008021006004001003007014004
  Base = -> Cut004008021006004001003007014003
  Tool = -> Extrusion047
FEATURE [Part::MultiFuse] Fusion005002002014004003003002009002010004002003006003008008004007002004008002005003003004013003004015003002008009002003
  Shapes = -> [Cut004008021006004001003007014004,Cut004008021006004001003007014002]
FEATURE [Part::Feature] Face043
  Placement = pos=(-22.7066,-0.0612293,5.22621e-08) rot=(0,0,1;0rad)
  shape: bbox 2.039e-07 x 54 x 2 mm, 1 faces, 0 solids (baked)
FEATURE [Part::Extrusion] Extrusion048
  Base = -> Face043
  Dir = (-0.9625,2e-16,-1.87204e-09)
  DirMode = 0
  FaceMakerClass = Part::FaceMakerBullseye
  LengthFwd = 0
  LengthRev = 0
  Solid = true
  Symmetric = false
FEATURE [Part::Feature] Face044
  Placement = pos=(-22.7066,-0.0612293,5.22621e-08) rot=(0,0,1;0rad)
  shape: bbox 2.039e-07 x 54 x 2 mm, 1 faces, 0 solids (baked)
FEATURE [Part::Extrusion] Extrusion049
  Base = -> Face044
  Dir = (0.9625,-2e-16,1.87204e-09)
  DirMode = 0
  FaceMakerClass = Part::FaceMakerBullseye
  LengthFwd = 0
  LengthRev = 0
  Solid = true
  Symmetric = false
FEATURE [Part::MultiFuse] Fusion005002002014004003003002009002010004002003006003008008004007002004008002005003003004013003004015003002008009002004
  Shapes = -> [Cut004008021006004001003007009,Extrusion049,Extrusion048]
FEATURE [Part::Part2DObjectPython] Rectangle010  # Draft 2D object (typed FeaturePython)
  ChamferSize = 0
  Columns = 1
  FilletRadius = 0
  Height = 137.648
  Length = 30.782
  MakeFace = true
  Placement = pos=(77.7493,-180.035,-182.571) rot=(0,0,1;0rad)
  Rows = 1
  Support = -> [Cut004008021006004001003007014001]
FEATURE [Part::FeaturePython] Slice  # WARN: FeaturePython — macro-defined, semantics opaque (R4)
  Base = -> Cut004008021006004001003007014001
  Mode = 1
  Tolerance = 0
  Tools = -> [Rectangle010]
FEATURE [Part::FeaturePython] Slice_child0  label="Slice.0"  # WARN: FeaturePython — macro-defined, semantics opaque (R4)
  Base = -> Slice
  FilterType = 1
  Invert = false
  OverrideMaxVal = 0
  WindowFrom = 80
  WindowTo = 100
  items = 0
FEATURE [Part::FeaturePython] Slice_child1  label="Slice.1"  # WARN: FeaturePython — macro-defined, semantics opaque (R4)
  Base = -> Slice
  FilterType = 1
  Invert = false
  OverrideMaxVal = 0
  Placement = pos=(-0.00417584,2.8e-14,-0.00629228) rot=(0,0,1;0rad)
  WindowFrom = 80
  WindowTo = 100
  items = 1
FEATURE [Part::MultiFuse] Fusion005002002014004003003002009002010004002003006003008008004007002004008002005003003004013003004015003002008009002005
  Shapes = -> [Slice_child1,Slice_child0]
FEATURE [App::DocumentObjectGroup] GrExplode_Slice  label="Exploded Slice"
  Group = -> [Fusion005002002014004003003002009002010004002003006003008008004007002004008002005003003004013003004015003002008009002005]
FEATURE [Part::Feature] Fusion005002002014004003003002009002010004002003006003008008004007002004008002005003003004013003004015003002008009002005001  label="Fusion005002002014004003003002009002010004002003006003008008004007002004008002005003003004013003004015003002008009002006"
  shape: bbox 187.2 x 15.6 x 18.67 mm, 55 faces (baked)
FEATURE [Part::Part2DObjectPython] Rectangle011  # Draft 2D object (typed FeaturePython)
  ChamferSize = 0
  Columns = 1
  FilletRadius = 0
  Height = 84.7958
  Length = 16.3872
  MakeFace = true
  Placement = pos=(107.676,-128.84,-175.823) rot=(0,1,0;3.1395rad)
  Rows = 1
  Support = -> [Fusion005002002014004003003002009002010004002003006003008008004007002004008002005003003004013003004015003002008009002005001]
FEATURE [Part::FeaturePython] Slice001  # WARN: FeaturePython — macro-defined, semantics opaque (R4)
  Base = -> Fusion005002002014004003003002009002010004002003006003008008004007002004008002005003003004013003004015003002008009002005001
  Mode = 1
  Tolerance = 0
  Tools = -> [Rectangle011]
FEATURE [Part::FeaturePython] Slice001_child0001  label="Slice001.001"  # WARN: FeaturePython — macro-defined, semantics opaque (R4)
  Base = -> Slice001
  FilterType = 1
  Invert = false
  OverrideMaxVal = 0
  WindowFrom = 80
  WindowTo = 100
  items = 0
FEATURE [App::DocumentObjectGroup] GrExplode_Slice001  label="Exploded Slice001"
  Group = -> [Slice001_child0001]
FEATURE [Part::FeaturePython] Slice001_child1  label="Slice001.1"  # WARN: FeaturePython — macro-defined, semantics opaque (R4)
  Base = -> Slice001
  FilterType = 1
  Invert = false
  OverrideMaxVal = 0
  Placement = pos=(0,-5.68e-14,-2) rot=(0,0,1;0rad)
  WindowFrom = 80
  WindowTo = 100
  items = 1
FEATURE [Part::Part2DObjectPython] Rectangle012  # Draft 2D object (typed FeaturePython)
  ChamferSize = 0
  Columns = 1
  FilletRadius = 0
  Height = 74.405
  Length = 14.7853
  MakeFace = true
  Placement = pos=(107.609,-136.638,-177.823) rot=(0,1,0;3.1395rad)
  Rows = 1
  Support = -> [Slice001_child1]
FEATURE [Part::FeaturePython] Slice002  # WARN: FeaturePython — macro-defined, semantics opaque (R4)
  Base = -> Slice001_child0001
  Mode = 1
  Tolerance = 0
  Tools = -> [Rectangle012]
FEATURE [Part::FeaturePython] Slice002_child0  label="Slice002.0"  # WARN: FeaturePython — macro-defined, semantics opaque (R4)
  Base = -> Slice002
  FilterType = 1
  Invert = false
  OverrideMaxVal = 0
  WindowFrom = 80
  WindowTo = 100
  items = 0
FEATURE [Part::MultiFuse] Fusion005002002014004003003002009002010004002003006003008008004007002004008002005003003004013003004015003002008009002005002
  Shapes = -> [Slice001_child1,Slice002_child0]
FEATURE [App::DocumentObjectGroup] GrExplode_Slice002  label="Exploded Slice002"
  Group = -> [Fusion005002002014004003003002009002010004002003006003008008004007002004008002005003003004013003004015003002008009002005002]
FEATURE [Part::Feature] Fusion005002002014004003003002009002010004002003006003008008004007002004008002005003003004013003004015003002008009002005002001  label="Fusion005002002014004003003002009002010004002003006003008008004007002004008002005003003004013003004015003002008009002005003"
  shape: bbox 187.2 x 15.6 x 18.67 mm, 57 faces (baked)
FEATURE [Part::Part2DObjectPython] Rectangle013  # Draft 2D object (typed FeaturePython)
  ChamferSize = 0
  Columns = 1
  FilletRadius = 0
  Height = 92.548
  Length = 16.4111
  MakeFace = true
  Placement = pos=(276.354,-45.1033,-175.817) rot=(0.999999,0,-0.001047;3.14159rad)
  Rows = 1
  Support = -> [Fusion005002002014004003003002009002010004002003006003008008004007002004008002005003003004013003004015003002008009002005002001]
FEATURE [Part::FeaturePython] Slice003  # WARN: FeaturePython — macro-defined, semantics opaque (R4)
  Base = -> Fusion005002002014004003003002009002010004002003006003008008004007002004008002005003003004013003004015003002008009002005002001
  Mode = 1
  Tolerance = 0
  Tools = -> [Rectangle013]
FEATURE [Part::FeaturePython] Slice003_child0  label="Slice003.0"  # WARN: FeaturePython — macro-defined, semantics opaque (R4)
  Base = -> Slice003
  FilterType = 1
  Invert = false
  OverrideMaxVal = 0
  WindowFrom = 80
  WindowTo = 100
  items = 0
FEATURE [App::DocumentObjectGroup] GrExplode_Slice003  label="Exploded Slice003"
  Group = -> [Slice003_child0]
FEATURE [Part::FeaturePython] Slice003_child1  label="Slice003.1"  # WARN: FeaturePython — macro-defined, semantics opaque (R4)
  Base = -> Slice003
  FilterType = 1
  Invert = false
  OverrideMaxVal = 0
  Placement = pos=(0,-5.68e-14,-2) rot=(0,0,1;0rad)
  WindowFrom = 80
  WindowTo = 100
  items = 1
FEATURE [Part::Part2DObjectPython] Rectangle014  # Draft 2D object (typed FeaturePython)
  ChamferSize = 0
  Columns = 1
  FilletRadius = 0
  Height = 67.8495
  Length = 12.8635
  MakeFace = true
  Placement = pos=(278.994,-88.0864,-177.823) rot=(0.999999,0,-0.001047;3.14159rad)
  Rows = 1
FEATURE [Part::FeaturePython] Slice004  # WARN: FeaturePython — macro-defined, semantics opaque (R4)
  Base = -> Slice003_child0
  Mode = 1
  Tolerance = 0
  Tools = -> [Rectangle014]
FEATURE [Part::FeaturePython] Slice004_child0  label="Slice004.0"  # WARN: FeaturePython — macro-defined, semantics opaque (R4)
  Base = -> Slice004
  FilterType = 1
  Invert = false
  OverrideMaxVal = 0
  WindowFrom = 80
  WindowTo = 100
  items = 0
FEATURE [Part::MultiFuse] Fusion005002002014004003003002009002010004002003006003008008004007002004008002005003003004013003004015003002008009002005002002
  Shapes = -> [Slice003_child1,Slice004_child0]
FEATURE [App::DocumentObjectGroup] GrExplode_Slice004  label="Exploded Slice004"
  Group = -> [Fusion005002002014004003003002009002010004002003006003008008004007002004008002005003003004013003004015003002008009002005002002]
FEATURE [Part::Feature] Fusion005002002014004003003002009002010004002003006003008008004007002004008002005003003004013003004015003002008009002005002002001  label="Fusion005002002014004003003002009002010004002003006003008008004007002004008002005003003004013003004015003002008009002005002003"
  shape: bbox 187.2 x 15.6 x 16.67 mm, 59 faces (baked)
